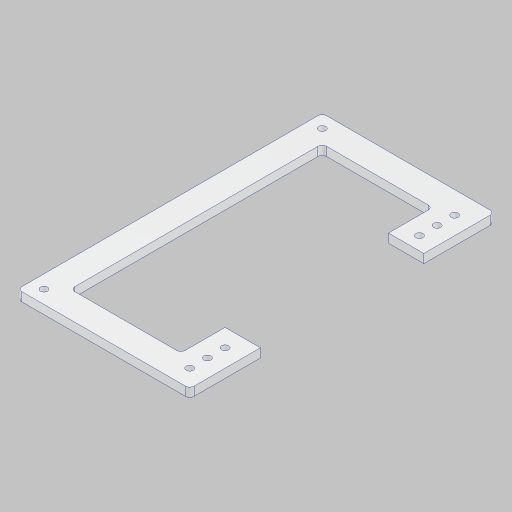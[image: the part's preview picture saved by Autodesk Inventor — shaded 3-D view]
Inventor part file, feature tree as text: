
AUTODESK INVENTOR PART (.ipt)
format: ipt  version: 2023.5 (Build 275446000, 446)  size: 178,176 bytes
history: native  units: in
note: dims shown in document units (in); Inventor stores cm internally (conversion verified against a paired STEP export)
features: sketch x2, hole x2, extrude x1, fillet x1
ambient origin geometry x8: Origin, YZ Plane, XZ Plane, XY Plane, X Axis, Y Axis, Z Axis, Center Point
bodies: Solid1 (feature_tree)
feature tree (6):
  sketch  "Sketch1"  dims[d0=3.125in d1=0.75in]
  extrude  "Extrusion1"  Depth=0.75in
  hole  "Hole3"  [1 undecoded]
  fillet  "Fillet1"  Radius=0.75in
  hole  "Hole4"  [1 undecoded]
  sketch  "Sketch3"  dims[d3=0.75in d4=3.125in d5=0.75in d6=0.25in d7=0.0in d8=7.125in d9=1.0in d10=0.75in d11=1.0in d12=0.75in d17=0.2in d18=0.25in d20=0.2in d21=0.5in d23=0.5in d38=0.2in d39=0.375in d40=0.375in d41=0.2in d42=0.375in d43=0.375in d44=0.201in d45=0.75in d46=0.375in d47=0.25in d48=0.5635in d49=1.0in d50=0.8108in d51=0.125in d52=0.5in d53=1.0in d54=2.0in d55=2.0in d56=1.0in d57=0.5in d58=0.5in d59=6.2992in d61=0.5in d62=0.3937in d64=1.0in d66=0.201in d67=0.75in d68=0.385in d69=0.25in d70=0.5635in d71=1.0in d72=0.8108in d24=1.0in d25=1.0in d26=0.15in d27=0.25in d28=0.375in d29=0.5635in d30=0.75in d31=0.8108in d32=0.0625in d33=0.75in d34=0.375in]
note: 2 required parameter values undecoded (feature->parameter linkage not recoverable at this tier; creation-order binding heuristic only, values carry confidence <= 0.55)
